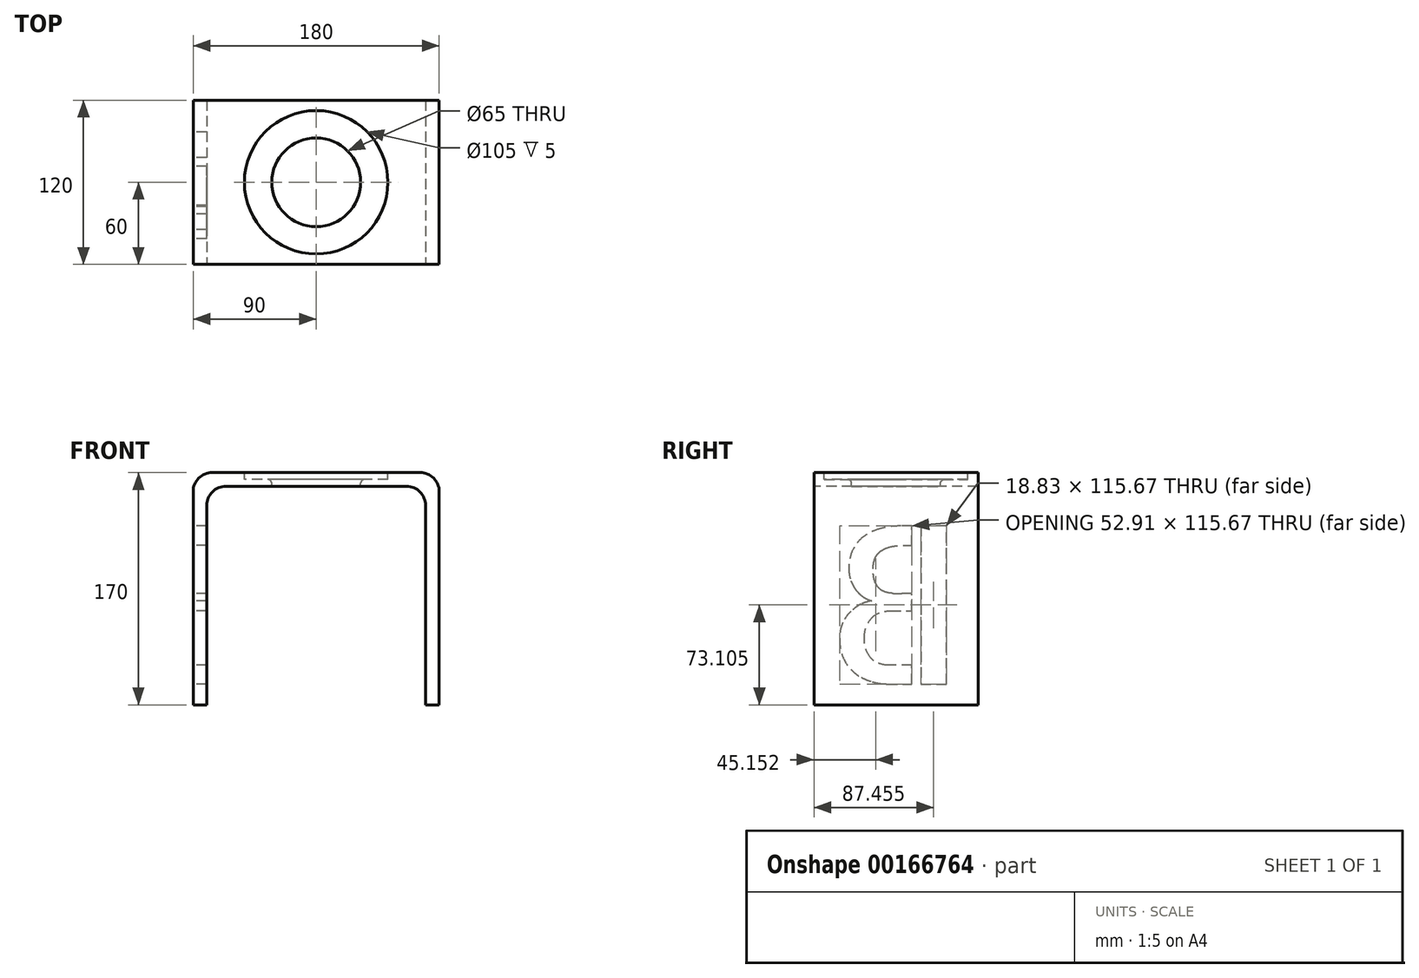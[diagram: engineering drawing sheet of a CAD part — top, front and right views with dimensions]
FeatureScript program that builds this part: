
annotation { "Feature Type Name" : "Feature", "Feature Type Description" : "" }
export const myFeature = defineFeature(function(context is Context, id is Id, definition is map)
    precondition{}
    {
        {
            var Q0;
            Q0=qCreatedBy(makeId("Front.planeOp"),FACE);
            var sketch = newSketch(context, id + "F0", { "sketchPlane" : qUnion([Q0])});
            skLineSegment(sketch, "E0", {"start": v(-80, 0) * mm, "end": v(-80, 160) * mm});
            skLineSegment(sketch, "E1", {"start": v(-80, 160) * mm, "end": v(0, 160) * mm});
            skLineSegment(sketch, "E2", {"start": v(0, 0) * mm, "end": v(0, 56.64) * mm, "construction": true});
            skLineSegment(sketch, "E3.0", {"start": v(-90, 170) * mm, "end": v(0, 170) * mm});
            skLineSegment(sketch, "E3.1", {"start": v(-90, 0) * mm, "end": v(-90, 170) * mm});
            skLineSegment(sketch, "E4", {"start": v(-90, 0) * mm, "end": v(-80, 0) * mm});
            skLineSegment(sketch, "E5.MirrorCS", {"start": v(80, 160) * mm, "end": v(0, 160) * mm});
            skLineSegment(sketch, "E6.MirrorCS", {"start": v(90, 170) * mm, "end": v(0, 170) * mm});
            skLineSegment(sketch, "E7.MirrorCS", {"start": v(90, 0) * mm, "end": v(80, 0) * mm});
            skLineSegment(sketch, "E8.MirrorCS", {"start": v(90, 0) * mm, "end": v(90, 170) * mm});
            skLineSegment(sketch, "E9.MirrorCS", {"start": v(80, 0) * mm, "end": v(80, 160) * mm});
            skSolve(sketch);
        }
        {
            var Q0;
            Q0 = qSketchRegion(id + "F0", true);
            extrude(context, id + "F1", {"entities" : qUnion([Q0]), "oppositeDirection" : true, "depth" : 120 * mm});
        }
        {
            var Q0;
            Q0=makeQuery(id+"F1.opExtrude","SWEPT_FACE",FACE,{"disambiguationData":[OSD([sQuery(id+"F0.wireOp",EDGE,"E3.0"),sQuery(id+"F0.wireOp",EDGE,"E6.MirrorCS")])]});
            var sketch = newSketch(context, id + "F2", { "sketchPlane" : qUnion([Q0])});
            skCircle(sketch, "E10", {"center": v(0, 60) * mm, "radius": 32.5 * mm});
            skPoint(sketch, "E11", {"position": v(0, 120) * mm});
            skPoint(sketch, "E12", {"position": v(90, 60) * mm});
            skSolve(sketch);
        }
        {
            var Q0;
            Q0 = qSketchRegion(id + "F2", true);
            extrude(context, id + "F3", {"entities" : qUnion([Q0]), "operationType" : NewBodyOperationType.REMOVE, "oppositeDirection" : true, "depth" : 10 * mm});
        }
        {
            var Q0;
            Q0=makeQuery(id+"F1.opExtrude","SWEPT_FACE",FACE,{"disambiguationData":[OSD([sQuery(id+"F0.wireOp",EDGE,"E3.0"),sQuery(id+"F0.wireOp",EDGE,"E6.MirrorCS")])]});
            var sketch = newSketch(context, id + "F4", { "sketchPlane" : qUnion([Q0])});
            skPoint(sketch, "E13", {"position": v(-90, 60) * mm});
            skCircle(sketch, "E14", {"center": v(0, 60) * mm, "radius": 52.5 * mm});
            skSolve(sketch);
        }
        {
            var Q0;
            Q0 = qSketchRegion(id + "F4", true);
            extrude(context, id + "F5", {"entities" : qUnion([Q0]), "operationType" : NewBodyOperationType.REMOVE, "oppositeDirection" : true, "depth" : 5 * mm});
        }
        {
            var Q0;
            Q0=makeQuery(id+"F5.boolean.opBoolean","INTERSECT",EDGE,{"derivedFrom":[makeQuery(id+"F3.boolean.opBoolean","COPY",FACE,{"derivedFrom":makeQuery(id+"F3.opExtrude","SWEPT_FACE",FACE,{"disambiguationData":[OSD([sQuery(id+"F2.wireOp",EDGE,"E10")])]})}),makeQuery(id+"F5.opExtrude","CAP_FACE",FACE,{"disambiguationData":[OSD([sQuery(id+"F4.wireOp",EDGE,"E14")])],"isStart":false})]});
            var Q1;
            Q1=makeQuery(id+"F5.boolean.opBoolean","COPY",EDGE,{"derivedFrom":makeQuery(id+"F5.opExtrude","CAP_EDGE",EDGE,{"disambiguationData":[OSD([sQuery(id+"F4.wireOp",EDGE,"E14")])],"isStart":true})});
            fillet(context, id + "F6", {"entities" : qUnion([Q0, Q1]), "radius" : 3 * mm, "tangentPropagation" : true, "allowEdgeOverflow" : false});
        }
        {
            var Q0;
            Q0=makeQuery(id+"F1.opExtrude","SWEPT_EDGE",EDGE,{"disambiguationData":[OSD([sQuery(id+"F0.wireOp",EDGE,"E6.MirrorCS"),sQuery(id+"F0.wireOp",EDGE,"E8.MirrorCS")])]});
            var Q1;
            Q1=makeQuery(id+"F1.opExtrude","SWEPT_EDGE",EDGE,{"disambiguationData":[OSD([sQuery(id+"F0.wireOp",EDGE,"E3.0"),sQuery(id+"F0.wireOp",EDGE,"E3.1")])]});
            var Q2;
            Q2=makeQuery(id+"F1.opExtrude","SWEPT_EDGE",EDGE,{"disambiguationData":[OSD([sQuery(id+"F0.wireOp",EDGE,"E5.MirrorCS"),sQuery(id+"F0.wireOp",EDGE,"E9.MirrorCS")])]});
            var Q3;
            Q3=makeQuery(id+"F1.opExtrude","SWEPT_EDGE",EDGE,{"disambiguationData":[OSD([sQuery(id+"F0.wireOp",EDGE,"E0"),sQuery(id+"F0.wireOp",EDGE,"E1")])]});
            fillet(context, id + "F7", {"entities" : qUnion([Q0, Q1, Q2, Q3]), "radius" : 14 * mm, "tangentPropagation" : true, "allowEdgeOverflow" : false});
        }
        {
            var Q0;
            Q0=makeQuery(id+"F1.opExtrude","SWEPT_FACE",FACE,{"disambiguationData":[OSD([sQuery(id+"F0.wireOp",EDGE,"E3.1")])]});
            var sketch = newSketch(context, id + "F8", { "sketchPlane" : qUnion([Q0])});
            skText(sketch, "E15", { "text": "B", "fontName": "AllertaStencil-Regular.ttf"});
            const initialGuessF8  = {"E15": [-0.11194, 0.01527, 1, 0, 0.11572]};
            skSetInitialGuess(sketch, initialGuessF8);
            skSolve(sketch);
        }
        {
            var Q0;
            Q0 = qSketchRegion(id + "F8", true);
            extrude(context, id + "F9", {"entities" : qUnion([Q0]), "operationType" : NewBodyOperationType.REMOVE, "oppositeDirection" : true, "depth" : 10 * mm});
        }
    });
